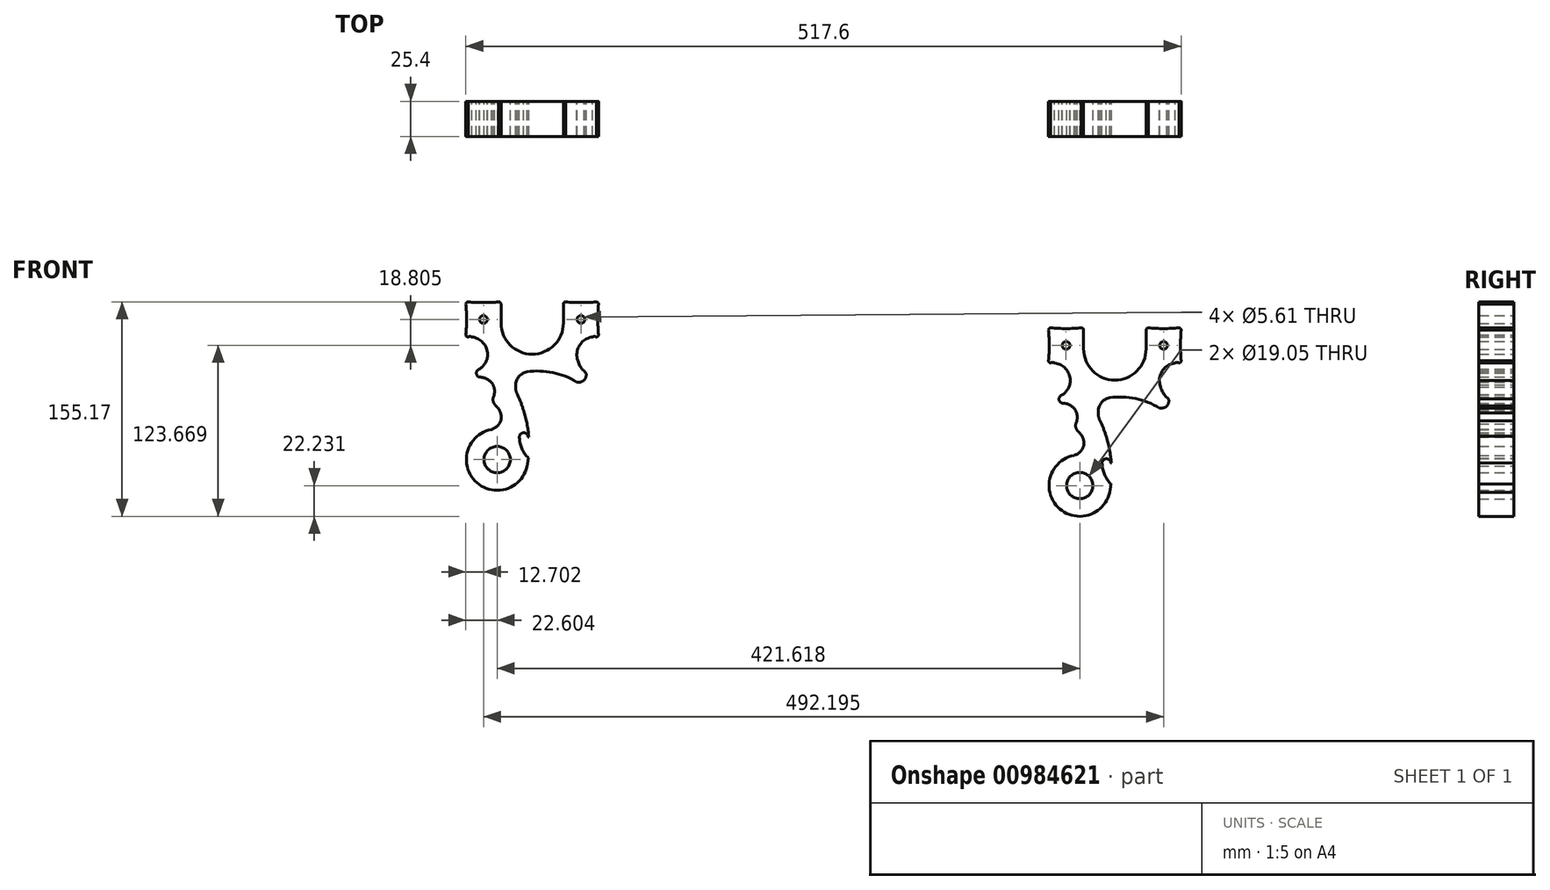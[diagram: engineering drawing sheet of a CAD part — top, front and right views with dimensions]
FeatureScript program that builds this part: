
annotation { "Feature Type Name" : "Feature", "Feature Type Description" : "" }
export const myFeature = defineFeature(function(context is Context, id is Id, definition is map)
    precondition{}
    {
        {
            var Q0;
            Q0=qCreatedBy(makeId("Front.planeOp"),FACE);
            var sketch = newSketch(context, id + "F0", { "sketchPlane" : qUnion([Q0])});
            skCircle(sketch, "E0", {"center": v(-25.39, -76.28) * mm, "radius": 9.53 * mm});
            skLineSegment(sketch, "E1.right", {"start": v(-22.59, 36.27) * mm, "end": v(-22.59, 22.59) * mm});
            skArc(sketch, "E2", {"start": v(-22.59, 22.59) * mm, "mid": v(-15.97, 6.62) * mm, "end": v(0, 0) * mm});
            skCircle(sketch, "E3", {"center": v(-35.29, 25.15) * mm, "radius": 2.8 * mm});
            skCircle(sketch, "E4.MirrorC", {"center": v(35.29, 25.15) * mm, "radius": 2.8 * mm});
            skLineSegment(sketch, "E5.MirrorCS", {"start": v(22.59, 36.27) * mm, "end": v(22.59, 22.59) * mm});
            skArc(sketch, "E6.MirrorCS", {"start": v(22.59, 22.59) * mm, "mid": v(15.97, 6.62) * mm, "end": v(0, 0) * mm});
            skArc(sketch, "E7", {"start": v(-47.99, 14.04) * mm, "mid": v(-47.52, 12.92) * mm, "end": v(-46.4, 12.45) * mm});
            skArc(sketch, "E8.MirrorC", {"start": v(-47.99, 36.27) * mm, "mid": v(-47.52, 37.39) * mm, "end": v(-46.4, 37.85) * mm});
            skArc(sketch, "E9.MirrorC", {"start": v(-22.59, 36.27) * mm, "mid": v(-23.05, 37.39) * mm, "end": v(-24.18, 37.85) * mm});
            skPoint(sketch, "E10.orphan", {"position": v(-47.99, 37.85) * mm});
            skPoint(sketch, "E11.orphan", {"position": v(-47.99, 12.45) * mm});
            skPoint(sketch, "E12.orphan", {"position": v(-22.59, 37.85) * mm});
            skArc(sketch, "E13.MirrorCS", {"start": v(47.99, 36.27) * mm, "mid": v(47.52, 37.39) * mm, "end": v(46.4, 37.85) * mm});
            skArc(sketch, "E14.MirrorCS", {"start": v(22.59, 36.27) * mm, "mid": v(23.05, 37.39) * mm, "end": v(24.18, 37.85) * mm});
            skArc(sketch, "E15.MirrorCS", {"start": v(47.99, 14.04) * mm, "mid": v(47.52, 12.92) * mm, "end": v(46.4, 12.45) * mm});
            skPoint(sketch, "E16.orphan", {"position": v(22.59, 37.85) * mm});
            skPoint(sketch, "E17.orphan", {"position": v(47.99, 37.85) * mm});
            skPoint(sketch, "E18.orphan", {"position": v(47.99, 12.45) * mm});
            skArc(sketch, "E19", {"start": v(-32.28, -0.11) * mm, "mid": v(-35.63, 8.34) * mm, "end": v(-43.74, 12.45) * mm});
            skArc(sketch, "E20", {"start": v(-38.44, -10.84) * mm, "mid": v(-33.94, -6.3) * mm, "end": v(-32.28, -0.11) * mm});
            skArc(sketch, "E21", {"start": v(-38.44, -10.84) * mm, "mid": v(-40.42, -13.83) * mm, "end": v(-38.18, -16.64) * mm});
            skArc(sketch, "E22.MirrorCS", {"start": v(32.28, -0.11) * mm, "mid": v(35.63, 8.34) * mm, "end": v(43.74, 12.45) * mm});
            skArc(sketch, "E23", {"start": v(32.28, -0.11) * mm, "mid": v(34.06, -7.56) * mm, "end": v(38.9, -13.49) * mm});
            skArc(sketch, "E24", {"start": v(37.72, -18.54) * mm, "mid": v(38.93, -16.16) * mm, "end": v(38.9, -13.49) * mm});
            skArc(sketch, "E25", {"start": v(32.28, -20.17) * mm, "mid": v(35.21, -20.07) * mm, "end": v(37.72, -18.54) * mm});
            skArc(sketch, "E26", {"start": v(32.28, -20.17) * mm, "mid": v(14.92, -13.33) * mm, "end": v(-3.73, -12.68) * mm});
            skArc(sketch, "E27", {"start": v(-3.73, -12.68) * mm, "mid": v(-9.91, -16.64) * mm, "end": v(-12.03, -23.68) * mm});
            skPoint(sketch, "E28.orphan", {"position": v(-35.29, 37.85) * mm});
            skPoint(sketch, "E29.orphan", {"position": v(-22.59, 25.15) * mm});
            skPoint(sketch, "E30.orphan", {"position": v(-35.29, 12.45) * mm});
            skPoint(sketch, "E31.orphan", {"position": v(-47.99, 25.15) * mm});
            skPoint(sketch, "E32.orphan", {"position": v(-22.59, 12.45) * mm});
            skPoint(sketch, "E33.orphan", {"position": v(22.59, 12.45) * mm});
            skPoint(sketch, "E34.orphan", {"position": v(35.29, 12.45) * mm});
            skPoint(sketch, "E35.orphan", {"position": v(47.99, 25.15) * mm});
            skPoint(sketch, "E36.orphan", {"position": v(35.29, 37.85) * mm});
            skPoint(sketch, "E37.orphan", {"position": v(22.59, 25.15) * mm});
            skArc(sketch, "E38", {"start": v(-28.21, -22.22) * mm, "mid": v(-32.43, -18.07) * mm, "end": v(-38.18, -16.64) * mm});
            skArc(sketch, "E39", {"start": v(-28.21, -31.5) * mm, "mid": v(-27.25, -26.86) * mm, "end": v(-28.21, -22.22) * mm});
            skArc(sketch, "E40", {"start": v(-28.21, -31.5) * mm, "mid": v(-28.33, -33.56) * mm, "end": v(-27.76, -35.54) * mm});
            skArc(sketch, "E41", {"start": v(-27.76, -35.54) * mm, "mid": v(-26.54, -37.12) * mm, "end": v(-25.13, -38.51) * mm});
            skArc(sketch, "E42", {"start": v(-22.6, -47.74) * mm, "mid": v(-22.82, -42.84) * mm, "end": v(-25.13, -38.51) * mm});
            skArc(sketch, "E43", {"start": v(-29.53, -54.44) * mm, "mid": v(-41.34, -91.77) * mm, "end": v(-3.68, -81.07) * mm});
            skArc(sketch, "E44", {"start": v(-29.53, -54.44) * mm, "mid": v(-25.22, -51.96) * mm, "end": v(-22.6, -47.74) * mm});
            skArc(sketch, "E45", {"start": v(-12.03, -23.68) * mm, "mid": v(-11.69, -26.59) * mm, "end": v(-10.68, -29.34) * mm});
            skArc(sketch, "E46", {"start": v(-6.3, -40.7) * mm, "mid": v(-8.24, -34.92) * mm, "end": v(-10.68, -29.34) * mm});
            skArc(sketch, "E47", {"start": v(-3.68, -81.07) * mm, "mid": v(-3.18, -78.11) * mm, "end": v(-2.8, -75.14) * mm});
            skArc(sketch, "E48", {"start": v(-2.94, -59.9) * mm, "mid": v(-6.24, -56.86) * mm, "end": v(-9.29, -60.15) * mm});
            skLineSegment(sketch, "E49", {"start": v(-2.94, -59.9) * mm, "end": v(-2.52, -59.9) * mm});
            skArc(sketch, "E50", {"start": v(-9.29, -60.15) * mm, "mid": v(-7.49, -68.27) * mm, "end": v(-2.8, -75.14) * mm});
            skArc(sketch, "E51.trimOffspring", {"start": v(-2.52, -59.9) * mm, "mid": v(-3.84, -50.19) * mm, "end": v(-6.3, -40.7) * mm});
            skArc(sketch, "E52", {"start": v(-47.99, 14.04) * mm, "mid": v(-47.5, 25.15) * mm, "end": v(-47.99, 36.27) * mm});
            skArc(sketch, "E53", {"start": v(-46.4, 37.85) * mm, "mid": v(-35.29, 37.37) * mm, "end": v(-24.18, 37.85) * mm});
            skArc(sketch, "E54.MirrorCS", {"start": v(46.4, 37.85) * mm, "mid": v(35.29, 37.37) * mm, "end": v(24.18, 37.85) * mm});
            skArc(sketch, "E55.MirrorCS", {"start": v(47.99, 14.04) * mm, "mid": v(47.5, 25.15) * mm, "end": v(47.99, 36.27) * mm});
            skArc(sketch, "E56", {"start": v(-43.74, 12.45) * mm, "mid": v(-45.07, 12.9) * mm, "end": v(-46.4, 12.45) * mm});
            skArc(sketch, "E57.MirrorCS", {"start": v(43.74, 12.45) * mm, "mid": v(45.07, 12.9) * mm, "end": v(46.4, 12.45) * mm});
            skCircle(sketch, "E58", {"center": v(396.23, -95.09) * mm, "radius": 9.53 * mm});
            skLineSegment(sketch, "E59.right", {"start": v(399.03, 17.46) * mm, "end": v(399.03, 3.78) * mm});
            skArc(sketch, "E60", {"start": v(399.03, 3.78) * mm, "mid": v(405.65, -12.19) * mm, "end": v(421.62, -18.8) * mm});
            skCircle(sketch, "E61", {"center": v(386.33, 6.35) * mm, "radius": 2.8 * mm});
            skCircle(sketch, "E62.MirrorC", {"center": v(456.9, 6.35) * mm, "radius": 2.8 * mm});
            skLineSegment(sketch, "E63.MirrorCS", {"start": v(444.2, 17.46) * mm, "end": v(444.2, 3.78) * mm});
            skArc(sketch, "E64.MirrorCS", {"start": v(444.2, 3.78) * mm, "mid": v(437.6, -12.19) * mm, "end": v(421.62, -18.8) * mm});
            skArc(sketch, "E65", {"start": v(373.63, -4.76) * mm, "mid": v(374.1, -5.89) * mm, "end": v(375.22, -6.35) * mm});
            skArc(sketch, "E66.MirrorC", {"start": v(373.63, 17.46) * mm, "mid": v(374.1, 18.58) * mm, "end": v(375.22, 19.05) * mm});
            skArc(sketch, "E67.MirrorC", {"start": v(399.03, 17.46) * mm, "mid": v(398.57, 18.58) * mm, "end": v(397.44, 19.05) * mm});
            skPoint(sketch, "E68.orphan", {"position": v(373.63, 19.05) * mm});
            skPoint(sketch, "E69.orphan", {"position": v(373.63, -6.35) * mm});
            skPoint(sketch, "E70.orphan", {"position": v(399.03, 19.05) * mm});
            skArc(sketch, "E71.MirrorCS", {"start": v(469.6, 17.46) * mm, "mid": v(469.14, 18.58) * mm, "end": v(468.02, 19.05) * mm});
            skArc(sketch, "E72.MirrorCS", {"start": v(444.2, 17.46) * mm, "mid": v(444.67, 18.58) * mm, "end": v(445.8, 19.05) * mm});
            skArc(sketch, "E73.MirrorCS", {"start": v(469.6, -4.76) * mm, "mid": v(469.14, -5.89) * mm, "end": v(468.02, -6.35) * mm});
            skPoint(sketch, "E74.orphan", {"position": v(444.2, 19.05) * mm});
            skPoint(sketch, "E75.orphan", {"position": v(469.6, 19.05) * mm});
            skPoint(sketch, "E76.orphan", {"position": v(469.6, -6.35) * mm});
            skArc(sketch, "E77", {"start": v(389.34, -18.92) * mm, "mid": v(385.99, -10.47) * mm, "end": v(377.88, -6.35) * mm});
            skArc(sketch, "E78", {"start": v(383.18, -29.65) * mm, "mid": v(387.68, -25.1) * mm, "end": v(389.34, -18.92) * mm});
            skArc(sketch, "E79", {"start": v(383.18, -29.65) * mm, "mid": v(381.2, -32.64) * mm, "end": v(383.43, -35.45) * mm});
            skArc(sketch, "E80.MirrorCS", {"start": v(453.9, -18.92) * mm, "mid": v(457.25, -10.47) * mm, "end": v(465.35, -6.35) * mm});
            skArc(sketch, "E81", {"start": v(453.9, -18.92) * mm, "mid": v(455.68, -26.36) * mm, "end": v(460.51, -32.3) * mm});
            skArc(sketch, "E82", {"start": v(459.33, -37.34) * mm, "mid": v(460.54, -34.96) * mm, "end": v(460.51, -32.3) * mm});
            skArc(sketch, "E83", {"start": v(453.9, -38.97) * mm, "mid": v(456.83, -38.87) * mm, "end": v(459.33, -37.34) * mm});
            skArc(sketch, "E84", {"start": v(453.9, -38.97) * mm, "mid": v(436.54, -32.14) * mm, "end": v(417.9, -31.49) * mm});
            skArc(sketch, "E85", {"start": v(417.9, -31.49) * mm, "mid": v(411.7, -35.45) * mm, "end": v(409.6, -42.48) * mm});
            skPoint(sketch, "E86.orphan", {"position": v(386.33, 19.05) * mm});
            skPoint(sketch, "E87.orphan", {"position": v(399.03, 6.35) * mm});
            skPoint(sketch, "E88.orphan", {"position": v(386.33, -6.35) * mm});
            skPoint(sketch, "E89.orphan", {"position": v(373.63, 6.35) * mm});
            skPoint(sketch, "E90.orphan", {"position": v(399.03, -6.35) * mm});
            skPoint(sketch, "E91.orphan", {"position": v(444.2, -6.35) * mm});
            skPoint(sketch, "E92.orphan", {"position": v(456.9, -6.35) * mm});
            skPoint(sketch, "E93.orphan", {"position": v(469.6, 6.35) * mm});
            skPoint(sketch, "E94.orphan", {"position": v(456.9, 19.05) * mm});
            skPoint(sketch, "E95.orphan", {"position": v(444.2, 6.35) * mm});
            skArc(sketch, "E96", {"start": v(393.4, -41.03) * mm, "mid": v(389.18, -36.87) * mm, "end": v(383.43, -35.45) * mm});
            skArc(sketch, "E97", {"start": v(393.4, -50.3) * mm, "mid": v(394.37, -45.67) * mm, "end": v(393.4, -41.03) * mm});
            skArc(sketch, "E98", {"start": v(393.4, -50.3) * mm, "mid": v(393.29, -52.36) * mm, "end": v(393.86, -54.35) * mm});
            skArc(sketch, "E99", {"start": v(393.86, -54.35) * mm, "mid": v(395.07, -55.92) * mm, "end": v(396.48, -57.32) * mm});
            skArc(sketch, "E100", {"start": v(399.02, -66.55) * mm, "mid": v(398.8, -61.64) * mm, "end": v(396.48, -57.32) * mm});
            skArc(sketch, "E101", {"start": v(392.1, -73.25) * mm, "mid": v(380.28, -110.57) * mm, "end": v(417.94, -99.88) * mm});
            skArc(sketch, "E102", {"start": v(392.1, -73.25) * mm, "mid": v(396.4, -70.76) * mm, "end": v(399.02, -66.55) * mm});
            skArc(sketch, "E103", {"start": v(409.6, -42.48) * mm, "mid": v(409.93, -45.4) * mm, "end": v(410.94, -48.15) * mm});
            skArc(sketch, "E104", {"start": v(415.32, -59.5) * mm, "mid": v(413.37, -53.73) * mm, "end": v(410.94, -48.15) * mm});
            skArc(sketch, "E105", {"start": v(417.94, -99.88) * mm, "mid": v(418.44, -96.92) * mm, "end": v(418.82, -93.95) * mm});
            skArc(sketch, "E106", {"start": v(418.67, -78.71) * mm, "mid": v(415.38, -75.66) * mm, "end": v(412.33, -78.96) * mm});
            skLineSegment(sketch, "E107", {"start": v(418.67, -78.71) * mm, "end": v(419.1, -78.71) * mm});
            skArc(sketch, "E108", {"start": v(412.33, -78.96) * mm, "mid": v(414.13, -87.08) * mm, "end": v(418.82, -93.95) * mm});
            skArc(sketch, "E109.trimOffspring", {"start": v(419.1, -78.71) * mm, "mid": v(417.78, -69) * mm, "end": v(415.32, -59.5) * mm});
            skArc(sketch, "E110", {"start": v(373.63, -4.76) * mm, "mid": v(374.12, 6.35) * mm, "end": v(373.63, 17.46) * mm});
            skArc(sketch, "E111", {"start": v(375.22, 19.05) * mm, "mid": v(386.33, 18.56) * mm, "end": v(397.44, 19.05) * mm});
            skArc(sketch, "E112.MirrorCS", {"start": v(468.02, 19.05) * mm, "mid": v(456.9, 18.56) * mm, "end": v(445.8, 19.05) * mm});
            skArc(sketch, "E113.MirrorCS", {"start": v(469.6, -4.76) * mm, "mid": v(469.12, 6.35) * mm, "end": v(469.6, 17.46) * mm});
            skArc(sketch, "E114", {"start": v(377.88, -6.35) * mm, "mid": v(376.55, -5.91) * mm, "end": v(375.22, -6.35) * mm});
            skArc(sketch, "E115.MirrorCS", {"start": v(465.35, -6.35) * mm, "mid": v(466.69, -5.91) * mm, "end": v(468.02, -6.35) * mm});
            skSolve(sketch);
        }
        {
            var Q0;
            Q0 = qSketchRegion(id + "F0", true);
            extrude(context, id + "F1", {"entities" : qUnion([Q0]), "domain" : OperationDomain.MODEL, "flatOperationType" : FlatOperationType.REMOVE, "depth" : 25.4 * mm, "offsetDistance" : 25.4 * mm});
        }
    });
